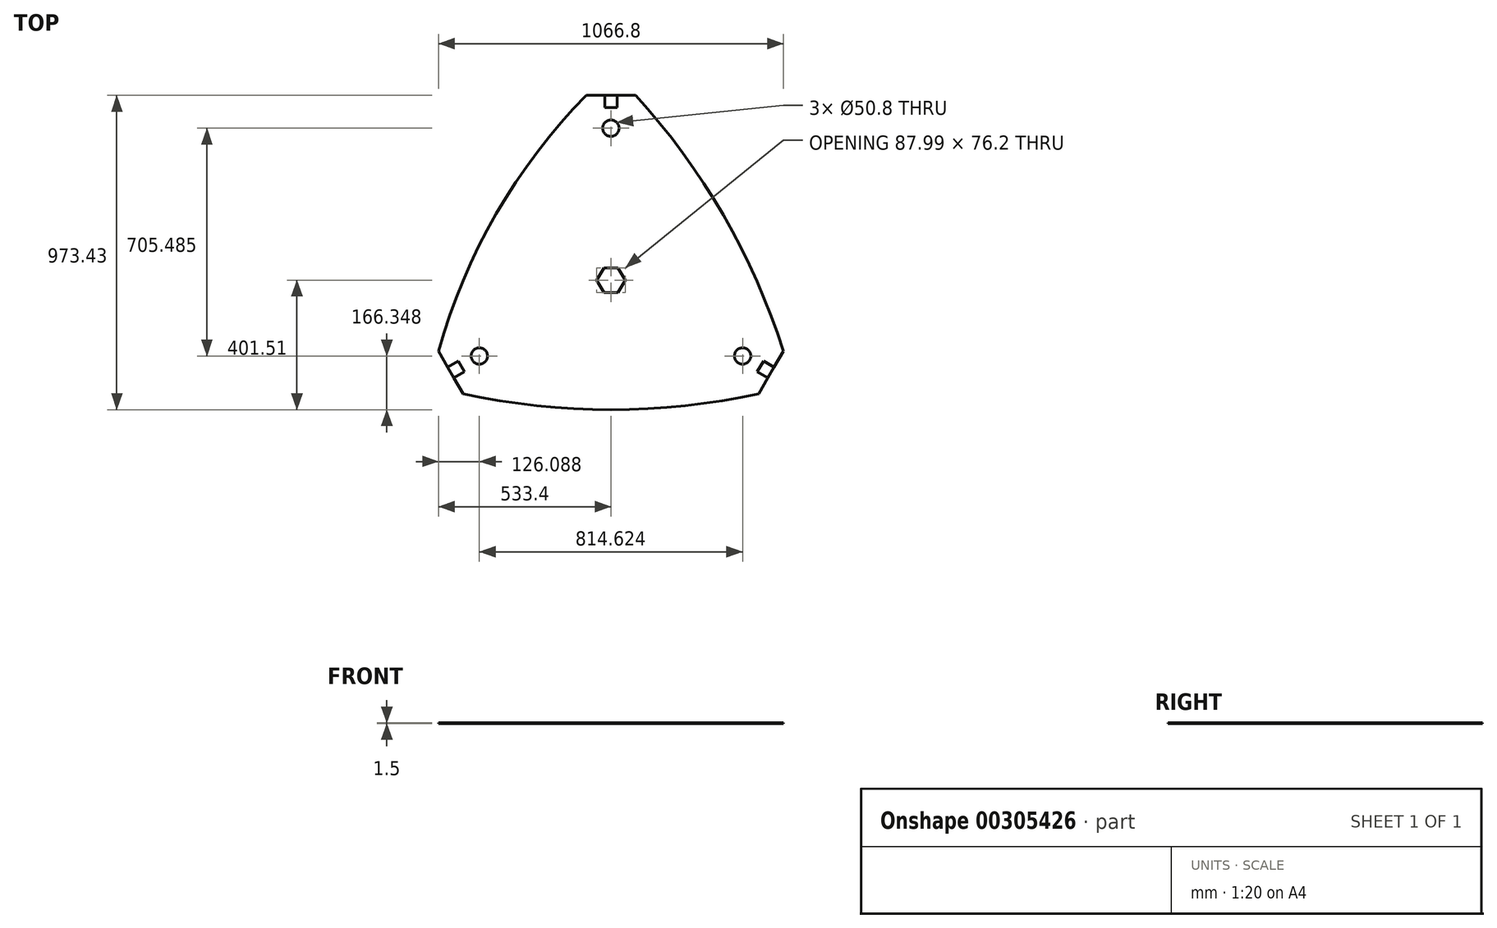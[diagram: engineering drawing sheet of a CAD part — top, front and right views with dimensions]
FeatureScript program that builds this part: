
annotation { "Feature Type Name" : "Feature", "Feature Type Description" : "" }
export const myFeature = defineFeature(function(context is Context, id is Id, definition is map)
    precondition{}
    {
        {
            var Q0;
            Q0=qCreatedBy(makeId("Top.planeOp"),FACE);
            var sketch = newSketch(context, id + "F0", { "sketchPlane" : qUnion([Q0])});
            skLineSegment(sketch, "E0", {"start": v(-533.4, -219.97) * mm, "end": v(-457.2, -351.95) * mm});
            skLineSegment(sketch, "E1", {"start": v(-457.2, -351.95) * mm, "end": v(457.2, -351.95) * mm, "construction": true});
            skLineSegment(sketch, "E2", {"start": v(457.2, -351.95) * mm, "end": v(533.4, -219.97) * mm});
            skLineSegment(sketch, "E3", {"start": v(533.4, -219.97) * mm, "end": v(76.2, 571.92) * mm, "construction": true});
            skLineSegment(sketch, "E4", {"start": v(76.2, 571.92) * mm, "end": v(-76.2, 571.92) * mm});
            skLineSegment(sketch, "E5", {"start": v(-76.2, 571.92) * mm, "end": v(-533.4, -219.97) * mm, "construction": true});
            skLineSegment(sketch, "E6", {"start": v(-304.8, 175.98) * mm, "end": v(0, 0) * mm, "construction": true});
            skLineSegment(sketch, "E7", {"start": v(0, -351.95) * mm, "end": v(0, 0) * mm, "construction": true});
            skLineSegment(sketch, "E8", {"start": v(304.8, 175.98) * mm, "end": v(0, 0) * mm, "construction": true});
            skArc(sketch, "E9", {"start": v(-76.2, 571.92) * mm, "mid": v(-355.1, 205.01) * mm, "end": v(-533.4, -219.97) * mm});
            skArc(sketch, "E10", {"start": v(-457.2, -351.95) * mm, "mid": v(0, -401.51) * mm, "end": v(457.2, -351.95) * mm});
            skArc(sketch, "E11", {"start": v(533.4, -219.97) * mm, "mid": v(347.72, 200.76) * mm, "end": v(76.2, 571.92) * mm});
            skLineSegment(sketch, "E12", {"start": v(-495.3, -285.96) * mm, "end": v(0, 0) * mm, "construction": true});
            skCircle(sketch, "E13", {"center": v(-407.31, -235.16) * mm, "radius": 25.4 * mm});
            skCircle(sketch, "E14.1.0", {"center": v(407.31, -235.16) * mm, "radius": 25.4 * mm});
            skCircle(sketch, "E14.2.0", {"center": v(0, 470.32) * mm, "radius": 25.4 * mm});
            skPoint(sketch, "E14.center", {"position": v(0, 0) * mm});
            skCircle(sketch, "E15.cCircle", {"center": v(0, 0) * mm, "radius": 38.1 * mm, "construction": true});
            skLineSegment(sketch, "E15.0", {"start": v(22, 38.1) * mm, "end": v(44, 0) * mm});
            skLineSegment(sketch, "E15.1", {"start": v(44, 0) * mm, "end": v(22, -38.1) * mm});
            skLineSegment(sketch, "E15.2", {"start": v(22, -38.1) * mm, "end": v(-22, -38.1) * mm});
            skLineSegment(sketch, "E15.3", {"start": v(-22, -38.1) * mm, "end": v(-44, 0) * mm});
            skLineSegment(sketch, "E15.4", {"start": v(-44, 0) * mm, "end": v(-22, 38.1) * mm});
            skLineSegment(sketch, "E15.5", {"start": v(-22, 38.1) * mm, "end": v(22, 38.1) * mm});
            skPoint(sketch, "E15.0.midPoint", {"position": v(33, 19.05) * mm});
            skLineSegment(sketch, "E16", {"start": v(-504.89, -269.35) * mm, "end": v(-471.9, -250.3) * mm});
            skLineSegment(sketch, "E17", {"start": v(-471.9, -250.3) * mm, "end": v(-452.72, -283.52) * mm});
            skLineSegment(sketch, "E18", {"start": v(-452.72, -283.52) * mm, "end": v(-485.71, -302.57) * mm});
            skLineSegment(sketch, "E19.1.0", {"start": v(471.9, -250.3) * mm, "end": v(504.89, -269.35) * mm});
            skLineSegment(sketch, "E19.1.1", {"start": v(452.72, -283.52) * mm, "end": v(471.9, -250.3) * mm});
            skLineSegment(sketch, "E19.1.2", {"start": v(485.71, -302.57) * mm, "end": v(452.72, -283.52) * mm});
            skLineSegment(sketch, "E19.2.0", {"start": v(-19.18, 533.82) * mm, "end": v(-19.18, 571.92) * mm});
            skLineSegment(sketch, "E19.2.1", {"start": v(19.18, 533.82) * mm, "end": v(-19.18, 533.82) * mm});
            skLineSegment(sketch, "E19.2.2", {"start": v(19.18, 571.92) * mm, "end": v(19.18, 533.82) * mm});
            skSolve(sketch);
        }
        {
            assignVariable(context, id + "F1", {"name" : "MaterialThickness", "anyValue" : .75});
        }
        {
            var Q0;
            Q0=makeQuery(id+"F0.imprint","IMPRINT",FACE,{"disambiguationData":[TD([[makeQuery(id+"F0.imprint","IMPRINT",EDGE,{"derivedFrom":sQuery(id+"F0.wireOp",EDGE,"E0")}),1.0]])]});
            extrude(context, id + "F2", {"entities" : qUnion([Q0]), "depth" : (2 * getVariable(context, 'MaterialThickness')) * mm});
        }
        {
            var Q0;
            {var subQ0=sQuery(id+"F0.wireOp",EDGE,"E16");Q0=makeQuery(id+"F0.imprint","IMPRINT",FACE,{"disambiguationData":[TD([[makeQuery(id+"F0.imprint","IMPRINT",EDGE,{"derivedFrom":subQ0}),-1.0]])]});}
            var Q1;
            {var subQ0=sQuery(id+"F0.wireOp",EDGE,"E19.1.0");Q1=makeQuery(id+"F0.imprint","IMPRINT",FACE,{"disambiguationData":[TD([[makeQuery(id+"F0.imprint","IMPRINT",EDGE,{"derivedFrom":subQ0}),-1.0]])]});}
            var Q2;
            {var subQ0=sQuery(id+"F0.wireOp",EDGE,"E19.2.0");Q2=makeQuery(id+"F0.imprint","IMPRINT",FACE,{"disambiguationData":[TD([[makeQuery(id+"F0.imprint","IMPRINT",EDGE,{"derivedFrom":subQ0}),-1.0]])]});}
            extrude(context, id + "F3", {"entities" : qUnion([Q0, Q1, Q2]), "operationType" : NewBodyOperationType.ADD, "depth" : (getVariable(context, 'MaterialThickness') * 4 / 3) * mm});
        }
    });
